# Revit family: НЕВАТОМ_Охладитель OFP-L_20220407
name_source: partatom
category: Оборудование
revit_build: Autodesk Revit 2017 (Build: 20170118_1100(x64)
units: mm (PartAtom-declared; Revit-internal decimal feet)

## family parameters
Всегда вертикально = Нет
На основе рабочей плоскости = Нет
Общий = Нет
При загрузке вырезать с полостями = Нет
Размер круглого соединителя = Использовать диаметр
Тип детали = Вставляется
Точка расчета площади = Нет

## types (18) — shared parameters
312 = 312 мм
5 = 5 мм
ADSK_Единица измерения = шт.
ADSK_Завод-изготовитель = NEVATOM
ADSK_Материал наименование = Оцинкованная сталь
ADSK_Наименование = ОХЛАДИТЕЛЬ ФРЕОНОВЫЙ
ADSK_Напряжение = 0 В
ADSK_Полная мощность = 0 кВт
ADSK_Размер_Ширина = 312 мм
ADSK_Ток = 0 А
Nevatom_URL = https://t.me
d = 20 мм
l = 30 мм
t = 2 мм
Материал корпуса = Материал корпуса

## per-type parameters (varying)
| type | A | ADSK_Марка | ADSK_Масса | ADSK_Масса_Текст | ADSK_Потеря давления воздуха | ADSK_Размер_Высота | ADSK_Размер_Длина | ADSK_Расход воздуха | B | C | C пр. сеч | D | D пр.сеч | E | F | G | K | N | Н |
| OFP 40-20/3 | 551 мм | OFP 40-20/3-L | 15.7 | 15,7 кг | 57.0 Па | 266 мм | 686 мм | 800.0 м³/ч | 266 мм | 220 мм | 200 мм | 420 мм | 400 мм | 90 мм | 64 мм | 12 мм | 686 мм | 14 | 16 мм |
| OFP 40-20/4 | 551 мм | OFP 40-20/4-L | 17 | 17,0 кг | 74.0 Па | 266 мм | 686 мм | 800.0 м³/ч | 266 мм | 220 мм | 200 мм | 420 мм | 400 мм | 90 мм | 64 мм | 12 мм | 686 мм | 14 | 16 мм |
| OFP 50-25/3 | 650 мм | OFP 50-25/3-L | 19.8 | 19,8 кг | 57.0 Па | 316 мм | 785 мм | 1250.0 м³/ч | 316 мм | 270 мм | 250 мм | 520 мм | 500 мм | 130 мм | 64 мм | 12 мм | 785 мм | 17 | 16 мм |
| OFP 50-25/4 | 650 мм | OFP 50-25/4-L | 20.8 | 20,8 кг | 74.0 Па | 316 мм | 785 мм | 1250.0 м³/ч | 316 мм | 270 мм | 250 мм | 520 мм | 500 мм | 130 мм | 64 мм | 12 мм | 785 мм | 17 | 16 мм |
| OFP 50-30/3 | 650 мм | OFP 50-30/3-L | 21.8 | 21,8 кг | 63.0 Па | 366 мм | 786 мм | 1600.0 м³/ч | 366 мм | 320 мм | 300 мм | 520 мм | 500 мм | 160 мм | 64 мм | 16 мм | 786 мм | 17 | 22 мм |
| OFP 50-30/4 | 650 мм | OFP 50-30/4-L | 22.7 | 22,7 кг | 82.0 Па | 366 мм | 786 мм | 1600.0 м³/ч | 366 мм | 320 мм | 300 мм | 520 мм | 500 мм | 160 мм | 64 мм | 16 мм | 786 мм | 17 | 22 мм |
| OFP 60-30/3 | 771 мм | OFP 60-30/3-L | 24.2 | 24,2 кг | 59.0 Па | 387 мм | 887 мм | 1850.0 м³/ч | 387 мм | 332 мм | 300 мм | 630 мм | 600 мм | 160 мм | 64 мм | 16 мм | 887 мм | 21 | 22 мм |
| OFP 60-30/4 | 771 мм | OFP 60-30/4-L | 25.4 | 25,4 кг | 78.0 Па | 387 мм | 887 мм | 1850.0 м³/ч | 387 мм | 332 мм | 300 мм | 630 мм | 600 мм | 160 мм | 64 мм | 16 мм | 887 мм | 21 | 22 мм |
| OFP 60-35/3 | 771 мм | OFP 60-35/3-L | 26 | 26,0 кг | 59.0 Па | 436 мм | 887 мм | 2150.0 м³/ч | 436 мм | 382 мм | 350 мм | 630 мм | 600 мм | 190 мм | 64 мм | 16 мм | 887 мм | 21 | 22 мм |
| OFP 60-35/4 | 771 мм | OFP 60-35/4-L | 27.4 | 27,4 кг | 77.0 Па | 436 мм | 887 мм | 2150.0 м³/ч | 436 мм | 382 мм | 350 мм | 630 мм | 600 мм | 190 мм | 64 мм | 16 мм | 887 мм | 21 | 22 мм |
| OFP 70-40/3 | 871 мм | OFP 70-40/3-L | 28.3 | 28,3 кг | 81.0 Па | 487 мм | 987 мм | 3500.0 м³/ч | 487 мм | 432 мм | 400 мм | 730 мм | 700 мм | 230 мм | 64 мм | 22 мм | 987 мм | 24 | 28 мм |
| OFP 70-40/4 | 871 мм | OFP 70-40/4-L | 32 | 32,0 кг | 106.0 Па | 487 мм | 987 мм | 3500.0 м³/ч | 487 мм | 432 мм | 400 мм | 730 мм | 700 мм | 230 мм | 64 мм | 22 мм | 987 мм | 24 | 28 мм |
| OFP 80-50/3 | 974 мм | OFP 80-50/3-L | 40 | 40,0 кг | 81.0 Па | 588 мм | 1087 мм | 5000.0 м³/ч | 588 мм | 530 мм | 500 мм | 830 мм | 800 мм | 290 мм | 64 мм | 22 мм | 1087 мм | 28 | 28 мм |
| OFP 80-50/4 | 974 мм | OFP 80-50/4-L | 40.3 | 40,3 кг | 107.0 Па | 588 мм | 1087 мм | 5000.0 м³/ч | 588 мм | 530 мм | 500 мм | 830 мм | 800 мм | 290 мм | 64 мм | 22 мм | 1087 мм | 28 | 28 мм |
| OFP 90-50/3 | 1080 мм | OFP 90-50/3-L | 42 | 42,0 кг | 78.0 Па | 588 мм | 1215 мм | 5500.0 м³/ч | 588 мм | 530 мм | 500 мм | 930 мм | 900 мм | 320 мм | 64 мм | 28 мм | 1215 мм | 31 | 35 мм |
| OFP 90-50/4 | 1080 мм | OFP 90-50/4-L | 43.3 | 43,3 кг | 103.0 Па | 588 мм | 1215 мм | 5500.0 м³/ч | 588 мм | 530 мм | 500 мм | 930 мм | 900 мм | 320 мм | 64 мм | 28 мм | 1215 мм | 31 | 35 мм |
| OFP 100-50/3 | 1170 мм | OFP 100-50/3-L | 45 | 45,0 кг | 76.0 Па | 588 мм | 1287 мм | 6000.0 м³/ч | 588 мм | 530 мм | 500 мм | 1030 мм | 1000 мм | 330 мм | 55 мм | 28 мм | 1287 мм | 34 | 35 мм |
| OFP 100-50/4 | 1170 мм | OFP 100-50/4-L | 46.3 | 46,3 кг | 101.0 Па | 588 мм | 1287 мм | 6000.0 м³/ч | 588 мм | 530 мм | 500 мм | 1030 мм | 1000 мм | 330 мм | 55 мм | 28 мм | 1287 мм | 34 | 35 мм |
